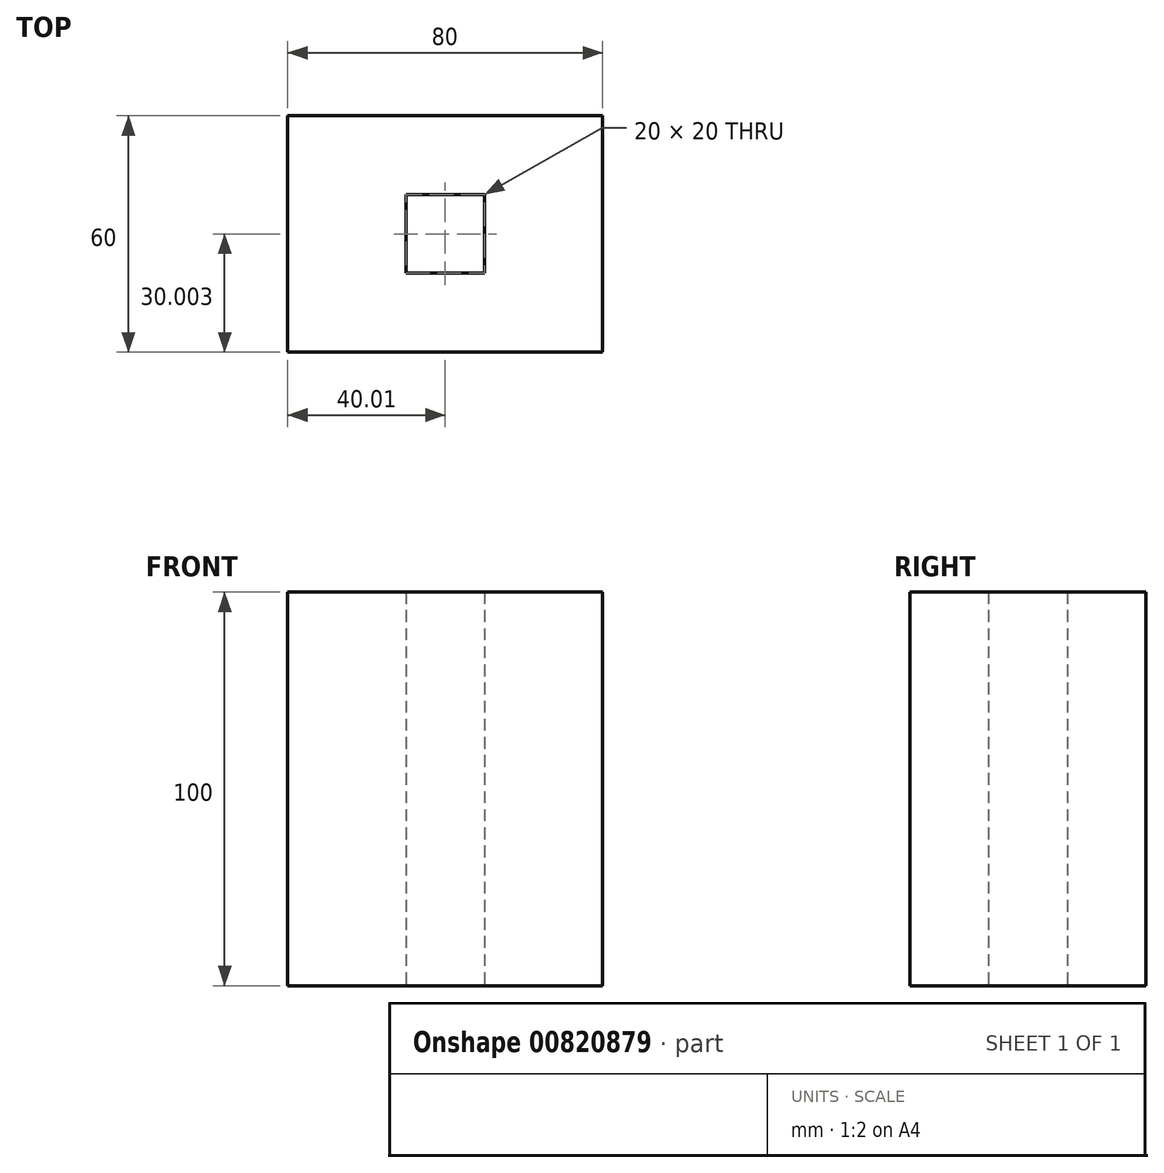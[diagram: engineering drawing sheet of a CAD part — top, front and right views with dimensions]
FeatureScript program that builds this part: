
annotation { "Feature Type Name" : "Feature", "Feature Type Description" : "" }
export const myFeature = defineFeature(function(context is Context, id is Id, definition is map)
    precondition{}
    {
        {
            var Q0;
            Q0=qCreatedBy(makeId("Top.planeOp"),FACE);
            var sketch = newSketch(context, id + "F0", { "sketchPlane" : qUnion([Q0])});
            skLineSegment(sketch, "E0", {"start": v(0, 0) * mm, "end": v(0, 60) * mm});
            skLineSegment(sketch, "E1", {"start": v(0, 60) * mm, "end": v(-80, 60) * mm});
            skLineSegment(sketch, "E2", {"start": v(-80, 60) * mm, "end": v(-80, 0) * mm});
            skLineSegment(sketch, "E3", {"start": v(-80, 0) * mm, "end": v(0, 0) * mm});
            skLineSegment(sketch, "E4.bottom", {"start": v(-29.99, 40) * mm, "end": v(-49.99, 40) * mm});
            skLineSegment(sketch, "E4.top", {"start": v(-29.99, 20) * mm, "end": v(-49.99, 20) * mm});
            skLineSegment(sketch, "E4.left", {"start": v(-29.99, 40) * mm, "end": v(-29.99, 20) * mm});
            skLineSegment(sketch, "E4.right", {"start": v(-49.99, 40) * mm, "end": v(-49.99, 20) * mm});
            skSolve(sketch);
        }
        {
            var Q0;
            Q0=makeQuery(id+"F0.imprint","IMPRINT",FACE,{"disambiguationData":[TD([[makeQuery(id+"F0.imprint","IMPRINT",EDGE,{"derivedFrom":sQuery(id+"F0.wireOp",EDGE,"E0")}),1.0]])]});
            extrude(context, id + "F1", {"entities" : qUnion([Q0]), "depth" : 100 * mm, "offsetDistance" : 25.4 * mm});
        }
    });
